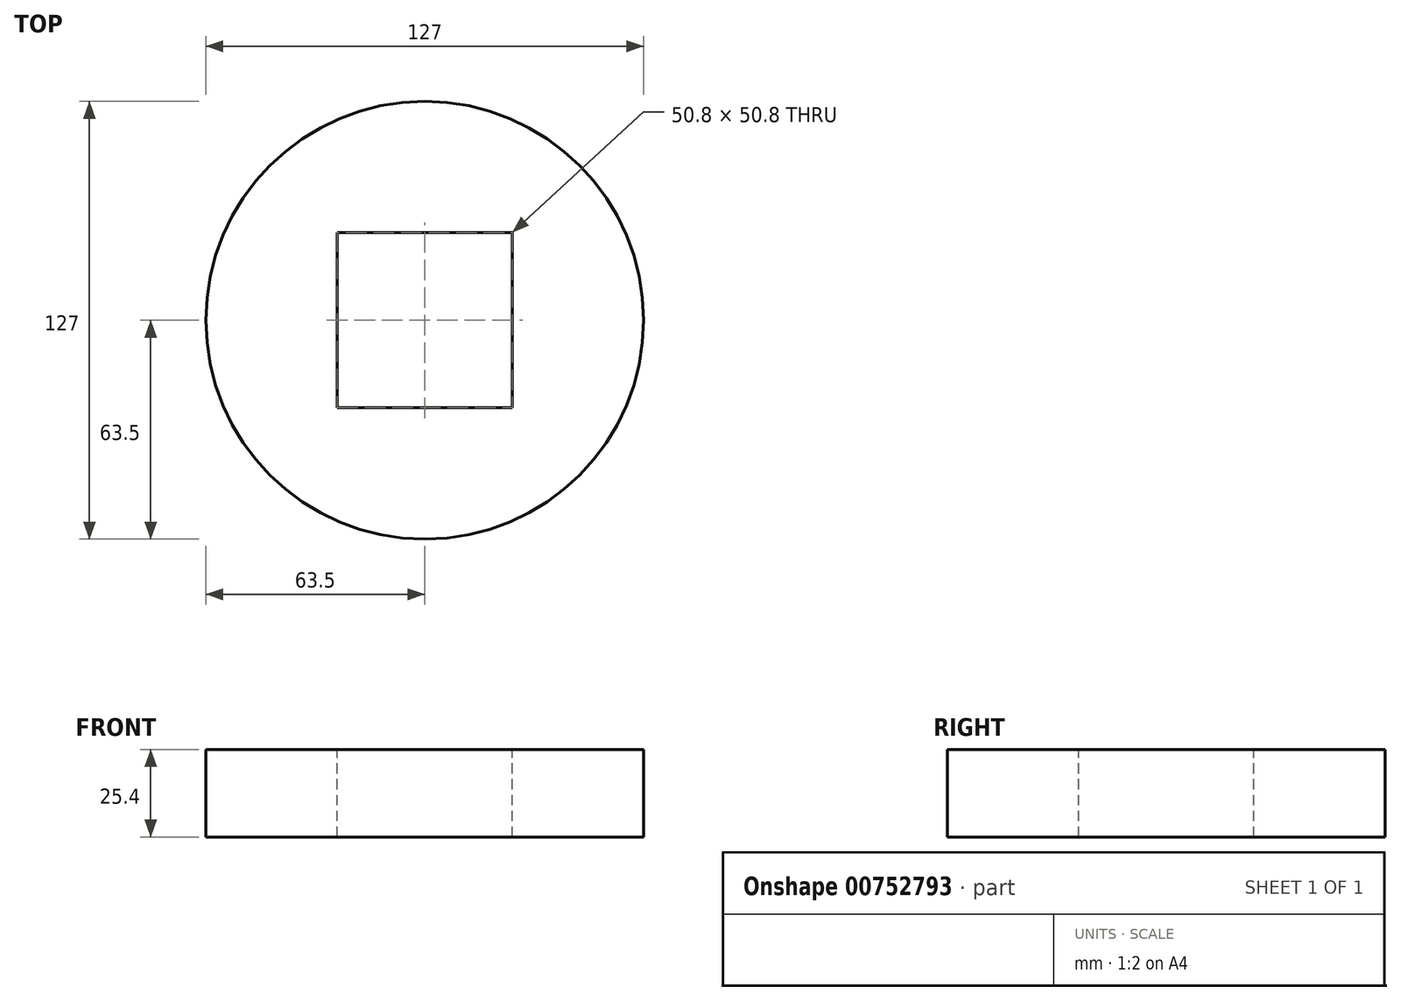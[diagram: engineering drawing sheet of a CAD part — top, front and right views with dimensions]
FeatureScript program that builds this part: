
annotation { "Feature Type Name" : "Feature", "Feature Type Description" : "" }
export const myFeature = defineFeature(function(context is Context, id is Id, definition is map)
    precondition{}
    {
        {
            var Q0;
            Q0=qCreatedBy(makeId("Top.planeOp"),FACE);
            var sketch = newSketch(context, id + "F0", { "sketchPlane" : qUnion([Q0])});
            skCircle(sketch, "E0", {"center": v(0, 0) * mm, "radius": 63.5 * mm});
            skSolve(sketch);
        }
        {
            var Q0;
            Q0 = qSketchRegion(id + "F0", true);
            extrude(context, id + "F1", {"entities" : qUnion([Q0]), "depth" : 25.4 * mm, "offsetDistance" : 25.4 * mm});
        }
        {
            var Q0;
            Q0=makeQuery(id+"F1.opExtrude","CAP_FACE",FACE,{"disambiguationData":[OSD([sQuery(id+"F0.wireOp",EDGE,"E0")])],"isStart":false});
            var sketch = newSketch(context, id + "F2", { "sketchPlane" : qUnion([Q0])});
            skLineSegment(sketch, "E1.bottom", {"start": v(-25.4, 25.4) * mm, "end": v(25.4, 25.4) * mm});
            skLineSegment(sketch, "E1.top", {"start": v(-25.4, -25.4) * mm, "end": v(25.4, -25.4) * mm});
            skLineSegment(sketch, "E1.left", {"start": v(-25.4, 25.4) * mm, "end": v(-25.4, -25.4) * mm});
            skLineSegment(sketch, "E1.right", {"start": v(25.4, 25.4) * mm, "end": v(25.4, -25.4) * mm});
            skPoint(sketch, "E1.middle", {"position": v(0, 0) * mm});
            skSolve(sketch);
        }
        {
            var Q0;
            Q0 = qSketchRegion(id + "F2", true);
            extrude(context, id + "F3", {"entities" : qUnion([Q0]), "operationType" : NewBodyOperationType.REMOVE, "endBound" : BoundingType.UP_TO_NEXT, "oppositeDirection" : true, "depth" : 25.4 * mm, "offsetDistance" : 25.4 * mm});
        }
    });
